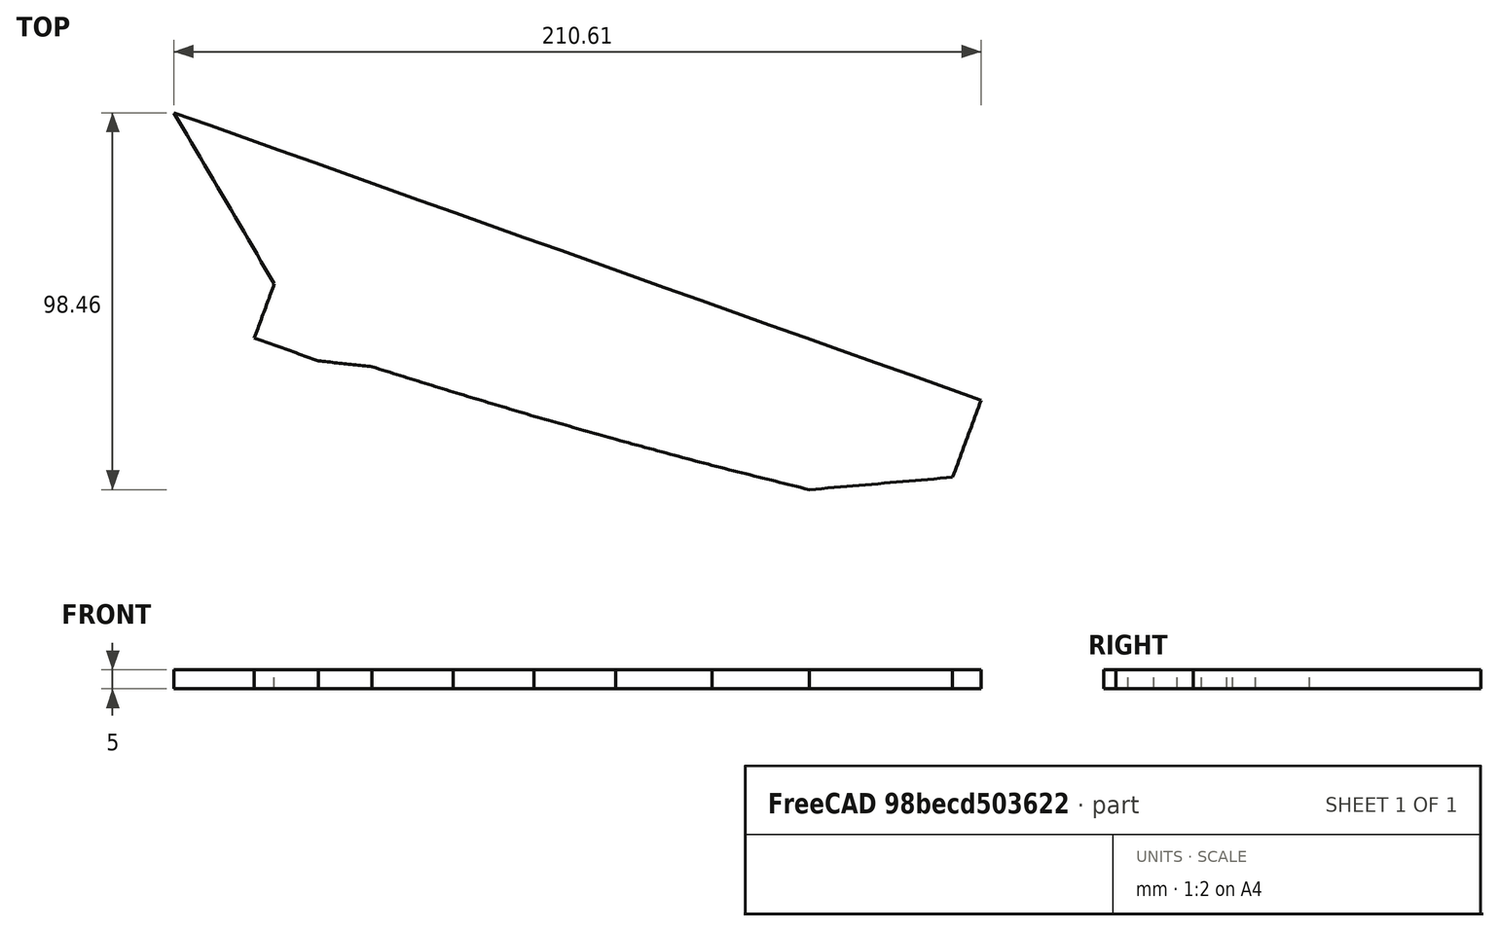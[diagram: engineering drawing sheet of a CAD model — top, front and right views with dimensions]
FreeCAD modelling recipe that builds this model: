
FCSTD DOCUMENT  (FreeCAD 0.19R)
Label: F-35_v2_parts_5
License: All rights reserved
LicenseURL: http://en.wikipedia.org/wiki/All_rights_reserved
objects: App::DocumentObjectGroup×2, PartDesign::CoordinateSystem×2, App::FeaturePython×1, Sketcher::SketchObject×1, PartDesign::Pad×1, PartDesign::Body×1, App::Part×1
note: 6 computed .brp shape members not serialized (recipe doc carries the construction recipe); baked Part::Feature solids carry a one-line shape summary decoded from their .brp

FEATURE [App::DocumentObjectGroup] Parts
FEATURE [PartDesign::CoordinateSystem] LCS_Origin
  AttacherType = Attacher::AttachEngine3D
  MapMode = 2
  Support = -> [X_Axis]
FEATURE [App::DocumentObjectGroup] Constraints
FEATURE [App::FeaturePython] Variables  # WARN: FeaturePython — macro-defined, semantics opaque (R4)
FEATURE [Sketcher::SketchObject] Sketch004
  FullyConstrained = false
  sketch-geometry (12):
    g0: BSplineCurve PolesCount=2 KnotsCount=2 Degree=1 IsPeriodic=0
    g1: BSplineCurve PolesCount=2 KnotsCount=2 Degree=1 IsPeriodic=0
    g2: BSplineCurve PolesCount=2 KnotsCount=2 Degree=1 IsPeriodic=0
    g3: BSplineCurve PolesCount=2 KnotsCount=2 Degree=1 IsPeriodic=0
    g4: BSplineCurve PolesCount=2 KnotsCount=2 Degree=1 IsPeriodic=0
    g5: BSplineCurve PolesCount=2 KnotsCount=2 Degree=1 IsPeriodic=0
    g6: BSplineCurve PolesCount=2 KnotsCount=2 Degree=1 IsPeriodic=0
    g7: BSplineCurve PolesCount=2 KnotsCount=2 Degree=1 IsPeriodic=0
    g8: BSplineCurve PolesCount=2 KnotsCount=2 Degree=1 IsPeriodic=0
    g9: BSplineCurve PolesCount=2 KnotsCount=2 Degree=1 IsPeriodic=0
    g10: BSplineCurve PolesCount=2 KnotsCount=2 Degree=1 IsPeriodic=0
    g11: BSplineCurve PolesCount=2 KnotsCount=2 Degree=1 IsPeriodic=0
  constraints (4):
    c: Coincident(g7,g8)
    c: Coincident(g8,g9)
    c: Coincident(g9,g10)
    c: Coincident(g10,g11)
FEATURE [PartDesign::Pad] Pad004
  Direction = (1,1,1)
  Length = 5
  Length2 = 100
  Profile = -> Sketch004
  Type = 0
FEATURE [PartDesign::Body] Body004  label="Part5"
  Group = -> [Sketch004,Pad004]
  Origin = -> Origin005
  Tip = -> Pad004
FEATURE [PartDesign::CoordinateSystem] LCS_1
  AttacherType = Attacher::AttachEngine3D
  AttachmentOffset = pos=(0,0,0) rot=(0,0,1;3.4828rad)
  MapMode = 7
  Placement = pos=(372.793,-216.163,0) rot=(0.985482,-0.16978,0;3.14159rad)
  Support = -> [Pad004]
FEATURE [App::Part] Model
  Configuration = 0
  Group = -> [LCS_Origin,Constraints,Variables,Body004,LCS_1]
  Origin = -> Origin
  Type = Assembly4 Model
